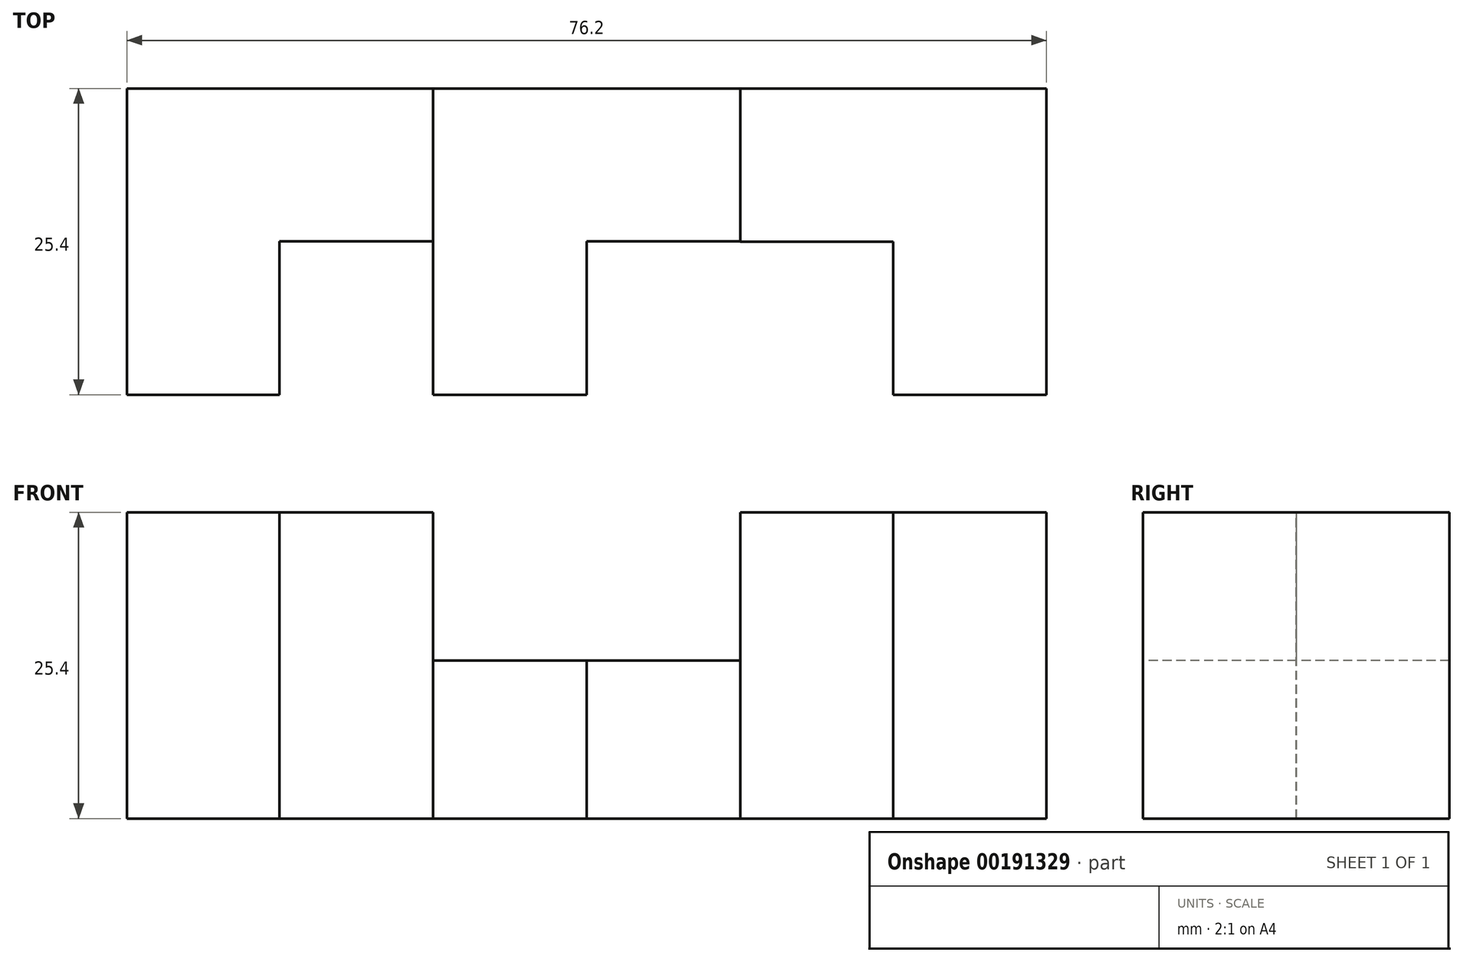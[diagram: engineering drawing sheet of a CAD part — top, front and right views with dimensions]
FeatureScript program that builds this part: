
annotation { "Feature Type Name" : "Feature", "Feature Type Description" : "" }
export const myFeature = defineFeature(function(context is Context, id is Id, definition is map)
    precondition{}
    {
        {
            var Q0;
            Q0=qCreatedBy(makeId("Top.planeOp"),FACE);
            var sketch = newSketch(context, id + "F0", { "sketchPlane" : qUnion([Q0])});
            skLineSegment(sketch, "E0.bottom", {"start": v(0, 0) * mm, "end": v(76.2, 0) * mm});
            skLineSegment(sketch, "E0.top", {"start": v(0, 25.4) * mm, "end": v(76.2, 25.4) * mm});
            skLineSegment(sketch, "E0.left", {"start": v(0, 0) * mm, "end": v(0, 25.4) * mm});
            skLineSegment(sketch, "E0.right", {"start": v(76.2, 0) * mm, "end": v(76.2, 25.4) * mm});
            skSolve(sketch);
        }
        {
            var Q0;
            Q0=makeQuery(id+"F0.imprint","IMPRINT",FACE,{"disambiguationData":[TD([[makeQuery(id+"F0.imprint","IMPRINT",EDGE,{"derivedFrom":sQuery(id+"F0.wireOp",EDGE,"E0.bottom")}),1.0]])]});
            extrude(context, id + "F1", {"entities" : qUnion([Q0]), "depth" : 25.4 * mm});
        }
        {
            var Q0;
            Q0=qCreatedBy(makeId("Front.planeOp"),FACE);
            var sketch = newSketch(context, id + "F2", { "sketchPlane" : qUnion([Q0])});
            skLineSegment(sketch, "E1.bottom", {"start": v(25.37, 25.82) * mm, "end": v(50.83, 25.82) * mm});
            skLineSegment(sketch, "E1.top", {"start": v(25.37, 13.1) * mm, "end": v(50.83, 13.1) * mm});
            skLineSegment(sketch, "E1.left", {"start": v(25.37, 25.82) * mm, "end": v(25.37, 13.1) * mm});
            skLineSegment(sketch, "E1.right", {"start": v(50.83, 25.82) * mm, "end": v(50.83, 13.1) * mm});
            skSolve(sketch);
        }
        {
            var Q0;
            Q0=makeQuery(id+"F2.imprint","IMPRINT",FACE,{"disambiguationData":[TD([[makeQuery(id+"F2.imprint","IMPRINT",EDGE,{"derivedFrom":sQuery(id+"F2.wireOp",EDGE,"E1.bottom")}),-1.0]])]});
            extrude(context, id + "F3", {"entities" : qUnion([Q0]), "operationType" : NewBodyOperationType.REMOVE, "oppositeDirection" : true, "depth" : 25.4 * mm});
        }
        {
            var Q0;
            {var subQ0=sQuery(id+"F0.wireOp",EDGE,"E0.bottom");var subQ1=sQuery(id+"F0.wireOp",EDGE,"E0.top");var subQ2=sQuery(id+"F0.wireOp",EDGE,"E0.left");Q0=makeQuery(id+"F3.boolean.opBoolean","SPLIT",FACE,{"disambiguationData":[TD([makeQuery(id+"F1.opExtrude","SWEPT_FACE",FACE,{"disambiguationData":[OSD([subQ2])]})])],"derivedFrom":makeQuery(id+"F1.opExtrude","CAP_FACE",FACE,{"disambiguationData":[OSD([subQ0,subQ1,subQ2,sQuery(id+"F0.wireOp",EDGE,"E0.right")])],"isStart":false})});}
            var sketch = newSketch(context, id + "F4", { "sketchPlane" : qUnion([Q0])});
            skLineSegment(sketch, "E2.bottom", {"start": v(25.37, 0) * mm, "end": v(12.65, 0) * mm});
            skLineSegment(sketch, "E2.top", {"start": v(25.37, 12.73) * mm, "end": v(12.65, 12.73) * mm});
            skLineSegment(sketch, "E2.left", {"start": v(25.37, 0) * mm, "end": v(25.37, 12.73) * mm});
            skLineSegment(sketch, "E2.right", {"start": v(12.65, 0) * mm, "end": v(12.65, 12.73) * mm});
            skSolve(sketch);
        }
        {
            var Q0;
            Q0=makeQuery(id+"F4.imprint","IMPRINT",FACE,{"disambiguationData":[TD([[makeQuery(id+"F4.imprint","IMPRINT",EDGE,{"derivedFrom":sQuery(id+"F4.wireOp",EDGE,"E2.bottom")}),1.0]])]});
            extrude(context, id + "F5", {"entities" : qUnion([Q0]), "operationType" : NewBodyOperationType.REMOVE, "oppositeDirection" : true, "depth" : 25.65 * mm});
        }
        {
            var Q0;
            {var subQ0=sQuery(id+"F0.wireOp",EDGE,"E0.bottom");var subQ1=sQuery(id+"F0.wireOp",EDGE,"E0.top");var subQ2=sQuery(id+"F0.wireOp",EDGE,"E0.right");Q0=makeQuery(id+"F3.boolean.opBoolean","SPLIT",FACE,{"disambiguationData":[TD([makeQuery(id+"F1.opExtrude","SWEPT_FACE",FACE,{"disambiguationData":[OSD([subQ2])]})])],"derivedFrom":makeQuery(id+"F1.opExtrude","CAP_FACE",FACE,{"disambiguationData":[OSD([subQ0,subQ1,sQuery(id+"F0.wireOp",EDGE,"E0.left"),subQ2])],"isStart":false})});}
            var sketch = newSketch(context, id + "F6", { "sketchPlane" : qUnion([Q0])});
            skPoint(sketch, "E3.oppositeSnap0", {"position": v(50.83, 12.7) * mm});
            skLineSegment(sketch, "E3.bottom", {"start": v(63.51, 0) * mm, "end": v(38.06, 0) * mm});
            skLineSegment(sketch, "E3.top", {"start": v(63.51, 12.7) * mm, "end": v(38.06, 12.7) * mm});
            skLineSegment(sketch, "E3.left", {"start": v(63.51, 0) * mm, "end": v(63.51, 12.7) * mm});
            skLineSegment(sketch, "E3.right", {"start": v(38.06, 0) * mm, "end": v(38.06, 12.7) * mm});
            skSolve(sketch);
        }
        {
            var Q0;
            {var subQ7=sQuery(id+"F6.wireOp",EDGE,"E3.left");Q0=makeQuery(id+"F6.imprint","IMPRINT",FACE,{"disambiguationData":[TD([[makeQuery(id+"F6.imprint","IMPRINT",EDGE,{"derivedFrom":subQ7}),1.0]])]});}
            extrude(context, id + "F7", {"entities" : qUnion([Q0]), "operationType" : NewBodyOperationType.REMOVE, "oppositeDirection" : true, "depth" : 25.65 * mm});
        }
        {
            var Q0;
            Q0=makeQuery(id+"F3.boolean.opBoolean","COPY",FACE,{"derivedFrom":makeQuery(id+"F3.opExtrude","SWEPT_FACE",FACE,{"disambiguationData":[OSD([sQuery(id+"F2.wireOp",EDGE,"E1.top")])]})});
            var sketch = newSketch(context, id + "F8", { "sketchPlane" : qUnion([Q0])});
            skLineSegment(sketch, "E4.bottom", {"start": v(50.83, 0) * mm, "end": v(38.1, 0) * mm});
            skLineSegment(sketch, "E4.top", {"start": v(50.83, 12.73) * mm, "end": v(38.1, 12.73) * mm});
            skLineSegment(sketch, "E4.left", {"start": v(50.83, 0) * mm, "end": v(50.83, 12.73) * mm});
            skLineSegment(sketch, "E4.right", {"start": v(38.1, 0) * mm, "end": v(38.1, 12.73) * mm});
            skSolve(sketch);
        }
        {
            var Q0;
            {var subQ1=sQuery(id+"F8.wireOp",EDGE,"E4.bottom");Q0=makeQuery(id+"F8.imprint","IMPRINT",FACE,{"disambiguationData":[TD([[makeQuery(id+"F8.imprint","IMPRINT",EDGE,{"derivedFrom":subQ1}),1.0]])]});}
            extrude(context, id + "F9", {"entities" : qUnion([Q0]), "operationType" : NewBodyOperationType.REMOVE, "oppositeDirection" : true, "depth" : 25.4 * mm});
        }
    });
